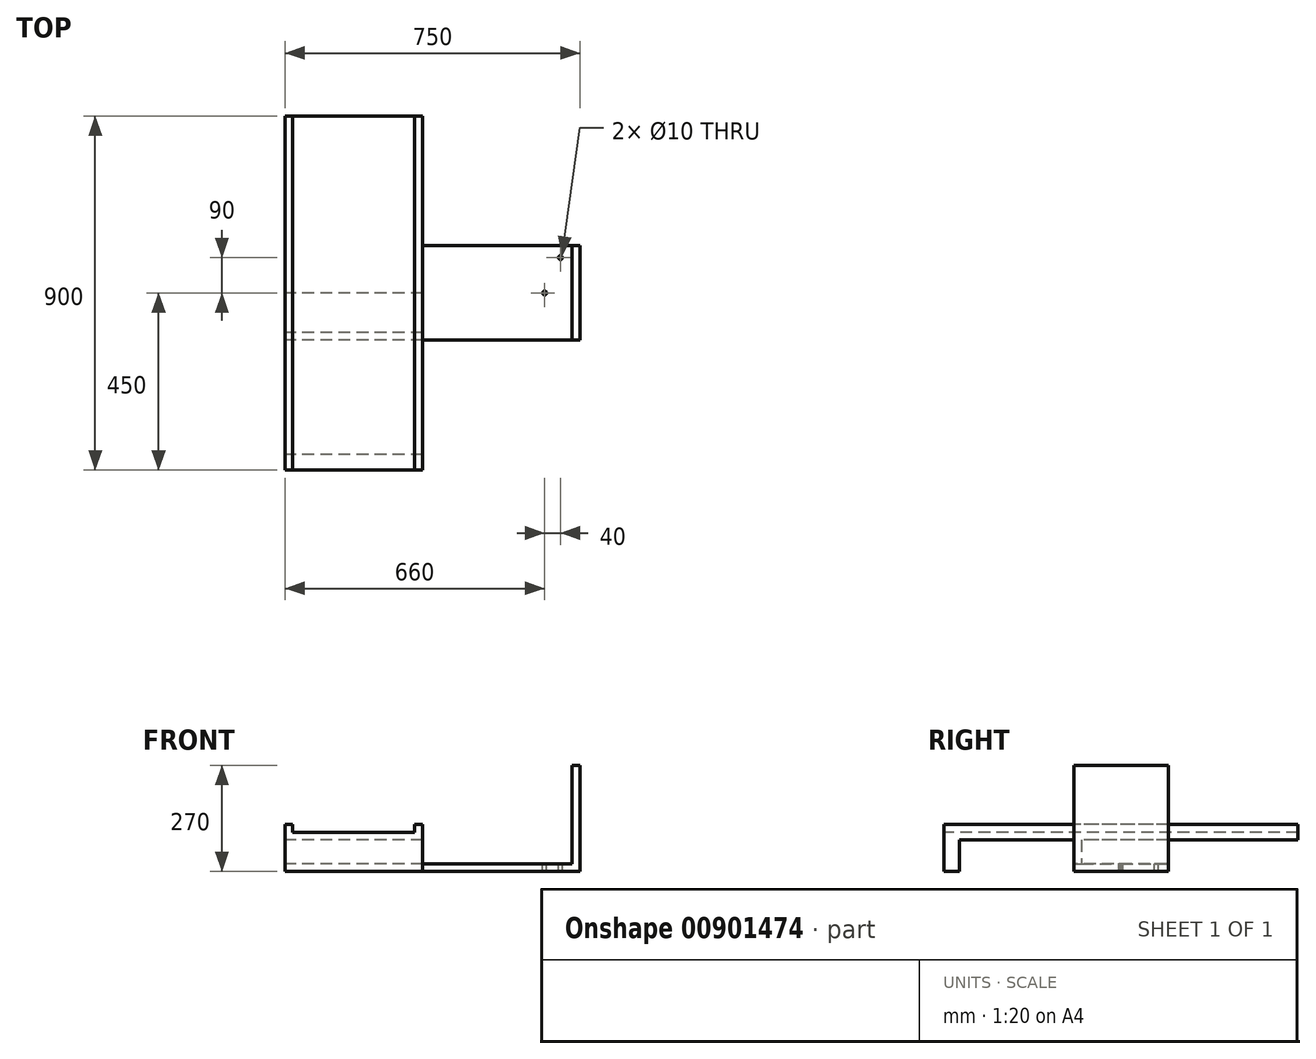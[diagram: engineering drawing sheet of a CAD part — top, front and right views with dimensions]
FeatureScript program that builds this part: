
annotation { "Feature Type Name" : "Feature", "Feature Type Description" : "" }
export const myFeature = defineFeature(function(context is Context, id is Id, definition is map)
    precondition{}
    {
        {
            var Q0;
            Q0=qCreatedBy(makeId("Top.planeOp"),FACE);
            var sketch = newSketch(context, id + "F0", { "sketchPlane" : qUnion([Q0])});
            skLineSegment(sketch, "E0.bottom", {"start": v(175, 450) * mm, "end": v(-175, 450) * mm});
            skLineSegment(sketch, "E0.top", {"start": v(175, -450) * mm, "end": v(-175, -450) * mm});
            skLineSegment(sketch, "E0.left", {"start": v(175, 450) * mm, "end": v(175, -450) * mm});
            skLineSegment(sketch, "E0.right", {"start": v(-175, 450) * mm, "end": v(-175, -450) * mm});
            skPoint(sketch, "E0.middle", {"position": v(0, 0) * mm});
            skSolve(sketch);
        }
        {
            var Q0;
            Q0 = qSketchRegion(id + "F0", true);
            extrude(context, id + "F1", {"entities" : qUnion([Q0]), "depth" : 20 * mm, "offsetDistance" : 25 * mm});
        }
        {
            var Q0;
            Q0=qCreatedBy(makeId("Right.planeOp"),FACE);
            var sketch = newSketch(context, id + "F2", { "sketchPlane" : qUnion([Q0])});
            skLineSegment(sketch, "E1.bottom", {"start": v(-120, 0) * mm, "end": v(-100, 0) * mm});
            skLineSegment(sketch, "E1.top", {"start": v(-120, -80) * mm, "end": v(-100, -80) * mm});
            skLineSegment(sketch, "E1.left", {"start": v(-120, 0) * mm, "end": v(-120, -80) * mm});
            skLineSegment(sketch, "E1.right", {"start": v(-100, 0) * mm, "end": v(-100, -80) * mm});
            skLineSegment(sketch, "E2.bottom", {"start": v(-100, -80) * mm, "end": v(0, -80) * mm});
            skLineSegment(sketch, "E2.top", {"start": v(-100, -60) * mm, "end": v(0, -60) * mm});
            skLineSegment(sketch, "E2.left", {"start": v(-100, -80) * mm, "end": v(-100, -60) * mm});
            skLineSegment(sketch, "E2.right", {"start": v(0, -80) * mm, "end": v(0, -60) * mm});
            skSolve(sketch);
        }
        {
            var Q0;
            Q0 = qSketchRegion(id + "F2", true);
            extrude(context, id + "F3", {"entities" : qUnion([Q0]), "operationType" : NewBodyOperationType.ADD, "endBound" : BoundingType.SYMMETRIC, "depth" : 350 * mm, "offsetDistance" : 25 * mm});
        }
        {
            var Q0;
            {var subQ0=sQuery(id+"F0.wireOp",EDGE,"E0.right");var subQ8=sQuery(id+"F0.wireOp",EDGE,"E0.left");var subQ9=sQuery(id+"F0.wireOp",EDGE,"E0.top");Q0=makeQuery(id+"F3.boolean.opBoolean","SPLIT",FACE,{"disambiguationData":[TD([makeQuery(id+"F1.opExtrude","SWEPT_FACE",FACE,{"disambiguationData":[OSD([subQ9])]})])],"derivedFrom":makeQuery(id+"F1.opExtrude","CAP_FACE",FACE,{"disambiguationData":[OSD([sQuery(id+"F0.wireOp",EDGE,"E0.bottom"),subQ9,subQ8,subQ0])],"isStart":true})});}
            var sketch = newSketch(context, id + "F4", { "sketchPlane" : qUnion([Q0])});
            skLineSegment(sketch, "E3.bottom", {"start": v(175, 450) * mm, "end": v(-175, 450) * mm});
            skLineSegment(sketch, "E3.top", {"start": v(175, 410) * mm, "end": v(-175, 410) * mm});
            skLineSegment(sketch, "E3.left", {"start": v(175, 450) * mm, "end": v(175, 410) * mm});
            skLineSegment(sketch, "E3.right", {"start": v(-175, 450) * mm, "end": v(-175, 410) * mm});
            skSolve(sketch);
        }
        {
            var Q0;
            Q0 = qSketchRegion(id + "F4", true);
            extrude(context, id + "F5", {"entities" : qUnion([Q0]), "operationType" : NewBodyOperationType.ADD, "depth" : 80 * mm, "offsetDistance" : 25 * mm});
        }
        {
            var Q0;
            Q0=makeQuery(id+"F1.opExtrude","CAP_FACE",FACE,{"disambiguationData":[OSD([sQuery(id+"F0.wireOp",EDGE,"E0.bottom"),sQuery(id+"F0.wireOp",EDGE,"E0.top"),sQuery(id+"F0.wireOp",EDGE,"E0.left"),sQuery(id+"F0.wireOp",EDGE,"E0.right")])],"isStart":false});
            var sketch = newSketch(context, id + "F6", { "sketchPlane" : qUnion([Q0])});
            skLineSegment(sketch, "E4.bottom", {"start": v(-175, 450) * mm, "end": v(-155, 450) * mm});
            skLineSegment(sketch, "E4.top", {"start": v(-175, -450) * mm, "end": v(-155, -450) * mm});
            skLineSegment(sketch, "E4.left", {"start": v(-175, 450) * mm, "end": v(-175, -450) * mm});
            skLineSegment(sketch, "E4.right", {"start": v(-155, 450) * mm, "end": v(-155, -450) * mm});
            skLineSegment(sketch, "E5.bottom", {"start": v(175, 450) * mm, "end": v(155, 450) * mm});
            skLineSegment(sketch, "E5.top", {"start": v(175, -450) * mm, "end": v(155, -450) * mm});
            skLineSegment(sketch, "E5.left", {"start": v(175, 450) * mm, "end": v(175, -450) * mm});
            skLineSegment(sketch, "E5.right", {"start": v(155, 450) * mm, "end": v(155, -450) * mm});
            skSolve(sketch);
        }
        {
            var Q0;
            Q0 = qSketchRegion(id + "F6", true);
            extrude(context, id + "F7", {"entities" : qUnion([Q0]), "operationType" : NewBodyOperationType.ADD, "depth" : 20 * mm, "offsetDistance" : 25 * mm});
        }
        {
            var Q0;
            {var subQ0=sQuery(id+"F4.wireOp",EDGE,"E3.left");var subQ1=sQuery(id+"F2.wireOp",EDGE,"E2.right");var subQ2=sQuery(id+"F2.wireOp",EDGE,"E2.top");var subQ3=sQuery(id+"F2.wireOp",EDGE,"E2.bottom");var subQ4=sQuery(id+"F2.wireOp",EDGE,"E1.right");var subQ5=sQuery(id+"F2.wireOp",EDGE,"E1.left");var subQ6=sQuery(id+"F2.wireOp",EDGE,"E1.top");var subQ7=sQuery(id+"F2.wireOp",EDGE,"E1.bottom");Q0=makeQuery(id+"F7.boolean.opBoolean","MERGE",FACE,{"derivedFrom":[makeQuery(id+"FmqejVucRUJoK7m_1.1.F5.boolean.opBoolean","MERGE",FACE,{"derivedFrom":[makeQuery(id+"F5.boolean.opBoolean","MERGE",FACE,{"derivedFrom":[makeQuery(id+"FAZT6p5FoR4vvCz_1.1.F3.boolean.opBoolean","MERGE",FACE,{"derivedFrom":[makeQuery(id+"F3.boolean.opBoolean","MERGE",FACE,{"derivedFrom":[makeQuery(id+"F1.opExtrude","SWEPT_FACE",FACE,{"disambiguationData":[OSD([sQuery(id+"F0.wireOp",EDGE,"E0.left")])]}),makeQuery(id+"F3.opExtrude","CAP_FACE",FACE,{"disambiguationData":[OSD([subQ7,subQ6,subQ5,subQ4,subQ3,subQ2,subQ1])],"isStart":false})]}),makeQuery(id+"FAZT6p5FoR4vvCz_1.1.F3.opExtrude","CAP_FACE",FACE,{"disambiguationData":[OSD([subQ7,subQ6,subQ5,subQ4,subQ3,subQ2,subQ1])],"isStart":false})]}),makeQuery(id+"F5.opExtrude","SWEPT_FACE",FACE,{"disambiguationData":[OSD([subQ0])]})]}),makeQuery(id+"FmqejVucRUJoK7m_1.1.F5.opExtrude","SWEPT_FACE",FACE,{"disambiguationData":[OSD([subQ0])]})]}),makeQuery(id+"F7.opExtrude","SWEPT_FACE",FACE,{"disambiguationData":[OSD([sQuery(id+"F6.wireOp",EDGE,"E5.left")])]})]});}
            var sketch = newSketch(context, id + "F8", { "sketchPlane" : qUnion([Q0])});
            skLineSegment(sketch, "E6.bottom", {"start": v(-120, -80) * mm, "end": v(120, -80) * mm});
            skLineSegment(sketch, "E6.top", {"start": v(-120, -60) * mm, "end": v(120, -60) * mm});
            skLineSegment(sketch, "E6.left", {"start": v(-120, -80) * mm, "end": v(-120, -60) * mm});
            skLineSegment(sketch, "E6.right", {"start": v(120, -80) * mm, "end": v(120, -60) * mm});
            skSolve(sketch);
        }
        {
            var Q0;
            Q0 = qSketchRegion(id + "F8", true);
            extrude(context, id + "F9", {"entities" : qUnion([Q0]), "operationType" : NewBodyOperationType.ADD, "depth" : 400 * mm, "offsetDistance" : 25 * mm});
        }
        {
            var Q0;
            {var subQ0=sQuery(id+"F2.wireOp",EDGE,"E2.top");Q0=makeQuery(id+"F9.boolean.opBoolean","MERGE",FACE,{"derivedFrom":[makeQuery(id+"FAZT6p5FoR4vvCz_1.1.F3.boolean.opBoolean","MERGE",FACE,{"derivedFrom":[makeQuery(id+"F3.opExtrude","SWEPT_FACE",FACE,{"disambiguationData":[OSD([subQ0])]}),makeQuery(id+"FAZT6p5FoR4vvCz_1.1.F3.opExtrude","SWEPT_FACE",FACE,{"disambiguationData":[OSD([subQ0])]})]}),makeQuery(id+"F9.opExtrude","SWEPT_FACE",FACE,{"disambiguationData":[OSD([sQuery(id+"F8.wireOp",EDGE,"E6.top")])]})]});}
            var sketch = newSketch(context, id + "F10", { "sketchPlane" : qUnion([Q0])});
            skLineSegment(sketch, "E7.bottom", {"start": v(575, 120) * mm, "end": v(555, 120) * mm});
            skLineSegment(sketch, "E7.top", {"start": v(575, -120) * mm, "end": v(555, -120) * mm});
            skLineSegment(sketch, "E7.left", {"start": v(575, 120) * mm, "end": v(575, -120) * mm});
            skLineSegment(sketch, "E7.right", {"start": v(555, 120) * mm, "end": v(555, -120) * mm});
            skSolve(sketch);
        }
        {
            var Q0;
            Q0 = qSketchRegion(id + "F10", true);
            extrude(context, id + "F11", {"entities" : qUnion([Q0]), "operationType" : NewBodyOperationType.ADD, "depth" : 250 * mm, "offsetDistance" : 25 * mm});
        }
        {
            var Q0;
            {var subQ0=sQuery(id+"F2.wireOp",EDGE,"E2.top");Q0=makeQuery(id+"F9.boolean.opBoolean","MERGE",FACE,{"derivedFrom":[makeQuery(id+"FAZT6p5FoR4vvCz_1.1.F3.boolean.opBoolean","MERGE",FACE,{"derivedFrom":[makeQuery(id+"F3.opExtrude","SWEPT_FACE",FACE,{"disambiguationData":[OSD([subQ0])]}),makeQuery(id+"FAZT6p5FoR4vvCz_1.1.F3.opExtrude","SWEPT_FACE",FACE,{"disambiguationData":[OSD([subQ0])]})]}),makeQuery(id+"F9.opExtrude","SWEPT_FACE",FACE,{"disambiguationData":[OSD([sQuery(id+"F8.wireOp",EDGE,"E6.top")])]})]});}
            var sketch = newSketch(context, id + "F12", { "sketchPlane" : qUnion([Q0])});
            skCircle(sketch, "E8", {"center": v(525, 90) * mm, "radius": 5 * mm});
            skCircle(sketch, "E9", {"center": v(485, 0) * mm, "radius": 5 * mm});
            skSolve(sketch);
        }
        {
            var Q0;
            Q0=makeQuery(id+"F12.imprint","IMPRINT",FACE,{"disambiguationData":[TD([[makeQuery(id+"F12.imprint","IMPRINT",EDGE,{"derivedFrom":sQuery(id+"F12.wireOp",EDGE,"E8")}),1.0]])]});
            var Q1;
            Q1=makeQuery(id+"F12.imprint","IMPRINT",FACE,{"disambiguationData":[TD([[makeQuery(id+"F12.imprint","IMPRINT",EDGE,{"derivedFrom":sQuery(id+"F12.wireOp",EDGE,"E9")}),1.0]])]});
            extrude(context, id + "F13", {"entities" : qUnion([Q0, Q1]), "operationType" : NewBodyOperationType.REMOVE, "endBound" : BoundingType.THROUGH_ALL, "oppositeDirection" : true, "depth" : 25 * mm, "offsetDistance" : 25 * mm});
        }
    });
